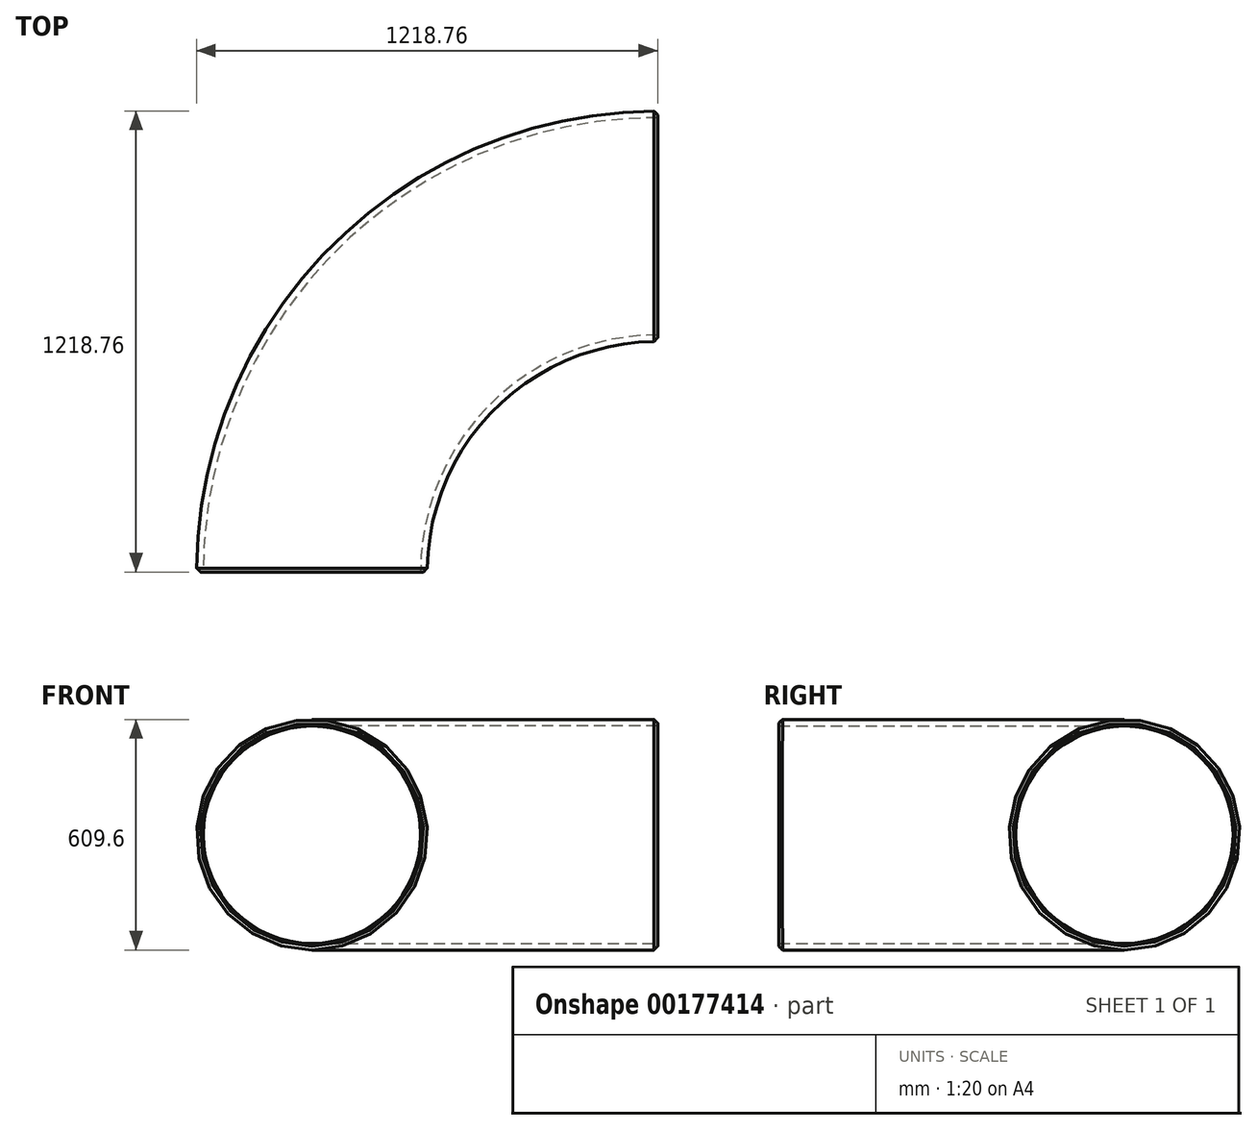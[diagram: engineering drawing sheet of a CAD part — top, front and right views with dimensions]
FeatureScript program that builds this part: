
annotation { "Feature Type Name" : "Feature", "Feature Type Description" : "" }
export const myFeature = defineFeature(function(context is Context, id is Id, definition is map)
    precondition{}
    {
        {
            var Q0;
            Q0=qCreatedBy(makeId("Top.planeOp"),FACE);
            var sketch = newSketch(context, id + "F0", { "sketchPlane" : qUnion([Q0])});
            skLineSegment(sketch, "E0", {"start": v(0, 0) * mm, "end": v(914, 0) * mm, "construction": true});
            skLineSegment(sketch, "E1", {"start": v(914, 0) * mm, "end": v(914, 914) * mm, "construction": true});
            skArc(sketch, "E2", {"start": v(0, 0) * mm, "mid": v(267.7, 646.3) * mm, "end": v(914, 914) * mm});
            skSolve(sketch);
        }
        {
            var Q0;
            Q0=qCreatedBy(makeId("Front.planeOp"),FACE);
            var sketch = newSketch(context, id + "F1", { "sketchPlane" : qUnion([Q0])});
            skCircle(sketch, "E3", {"center": v(0, 0) * mm, "radius": 304.8 * mm});
            skCircle(sketch, "E4", {"center": v(0, 0) * mm, "radius": 287.32 * mm});
            skSolve(sketch);
        }
        {
            var Q0;
            Q0=makeQuery(id+"F1.imprint","IMPRINT",FACE,{"disambiguationData":[TD([[makeQuery(id+"F1.imprint","IMPRINT",EDGE,{"derivedFrom":sQuery(id+"F1.wireOp",EDGE,"E3")}),1.0]])]});
            var Q1;
            Q1=sQuery(id+"F0.wireOp",EDGE,"E2");
            sweep(context, id + "F2", {"profiles" : qUnion([Q0]), "path" : qUnion([Q1])});
        }
        {
            var Q0;
            Q0=makeQuery(id+"F2.opSweep","CAP_EDGE",EDGE,{"disambiguationData":[OSD([sQuery(id+"F0.wireOp",VERTEX,"E2.start"),sQuery(id+"F1.wireOp",EDGE,"E3")])],"isStart":true});
            chamfer(context, id + "F3", {"entities" : qUnion([Q0]), "width" : 10 * mm, "tangentPropagation" : true});
        }
        {
            var Q0;
            Q0=makeQuery(id+"F2.opSweep","CAP_EDGE",EDGE,{"disambiguationData":[OSD([sQuery(id+"F0.wireOp",VERTEX,"E2.end"),sQuery(id+"F1.wireOp",EDGE,"E3")])],"isStart":false});
            chamfer(context, id + "F4", {"entities" : qUnion([Q0]), "width" : 10 * mm, "tangentPropagation" : true});
        }
    });
